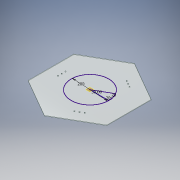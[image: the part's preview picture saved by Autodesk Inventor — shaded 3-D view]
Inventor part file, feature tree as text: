
AUTODESK INVENTOR PART (.ipt)
format: ipt  version: 2019 (Build 230136000, 136)  size: 177,152 bytes
history: native  units: mm
features: plane x2, extrude x2, sketch x2, pattern_circular x1
ambient origin geometry x8: Origin, YZ Plane, XZ Plane, XY Plane, X Axis, Y Axis, Z Axis, Center Point
bodies: Body1 (feature_tree)
feature tree (7):
  plane  "Work Plane2"
  plane  "Work Plane1"
  extrude  "Extrusion8"  Depth=37.5mm
  extrude  "Extrusion10"  Depth=3.0mm
  pattern_circular  "Circular Pattern2"  Count=2  [1 undecoded]
  sketch  "Sketch5"  dims[d2=150.0deg d3=160.0mm d4=20.0mm d5=4.5mm d6=20.0mm d8=20.0mm d9=20.0mm d11=20.0mm d14=10.0mm d15=10.0mm d16=60.0mm d17=40.0mm d18=30.0mm d20=360.0deg d22=96.0mm d45=45.0mm d46=120.0deg d47=50.0mm d48=90.0deg d49=50.0mm d50=30.0deg d51=30.0mm d53=360.0deg d72=125.0mm d77=3.0mm d78=0.0mm d79=150.0mm d80=5.0mm d81=19.995mm d82=5.0mm d83=19.995mm d84=5.0mm d90=5.0mm d91=3.0mm d92=0.0mm d93=30.0mm d94=360.0deg d96=200.0mm d97=20.0mm d98=30.0deg d99=20.0mm]
  sketch  "Sketch4"  dims[d0=75.0mm d1=37.5mm]
note: 1 required parameter value undecoded (feature->parameter linkage not recoverable at this tier; creation-order binding heuristic only, values carry confidence <= 0.55)
